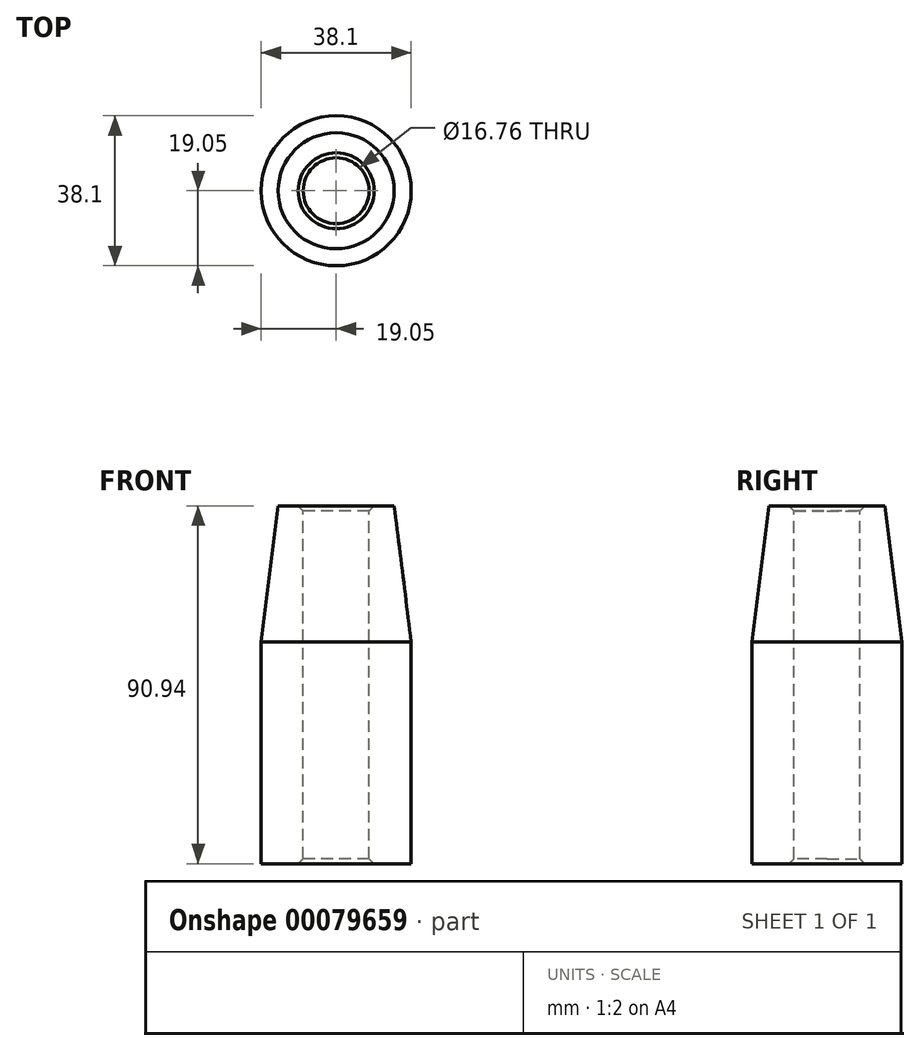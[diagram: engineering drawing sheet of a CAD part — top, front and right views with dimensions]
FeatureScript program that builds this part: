
annotation { "Feature Type Name" : "Feature", "Feature Type Description" : "" }
export const myFeature = defineFeature(function(context is Context, id is Id, definition is map)
    precondition{}
    {
        {
            var Q0;
            Q0=qCreatedBy(makeId("Front.planeOp"),FACE);
            var sketch = newSketch(context, id + "F0", { "sketchPlane" : qUnion([Q0])});
            skLineSegment(sketch, "E0", {"start": v(-8.38, 45.47) * mm, "end": v(-8.38, 0) * mm});
            skLineSegment(sketch, "E1", {"start": v(-8.38, 0) * mm, "end": v(-8.38, -45.47) * mm});
            skLineSegment(sketch, "E2", {"start": v(-19.05, 10.92) * mm, "end": v(-19.05, -45.47) * mm});
            skLineSegment(sketch, "E3", {"start": v(-8.38, 45.47) * mm, "end": v(-14.73, 45.47) * mm});
            skLineSegment(sketch, "E4", {"start": v(-14.73, 45.47) * mm, "end": v(-19.05, 10.92) * mm});
            skLineSegment(sketch, "E5", {"start": v(-19.05, -45.47) * mm, "end": v(-8.38, -45.47) * mm});
            skSolve(sketch);
        }
        {
            var Q0;
            Q0=qCreatedBy(makeId("Front.planeOp"),FACE);
            var sketch = newSketch(context, id + "F1", { "sketchPlane" : qUnion([Q0])});
            skLineSegment(sketch, "E6", {"start": v(0, 53.8) * mm, "end": v(0, -53.5) * mm, "construction": true});
            skSolve(sketch);
        }
        {
            var Q0;
            Q0=makeQuery(id+"F0.imprint","IMPRINT",FACE,{"disambiguationData":[TD([[makeQuery(id+"F0.imprint","IMPRINT",EDGE,{"derivedFrom":sQuery(id+"F0.wireOp",EDGE,"E0")}),-1.0]])]});
            var Q1;
            Q1=sQuery(id+"F1.wireOp",EDGE,"E6");
            revolve(context, id + "F2", {"entities" : qUnion([Q0]), "axis" : qUnion([Q1]), "revolveType" : RevolveType.FULL});
        }
        {
            var Q0;
            Q0=makeQuery(id+"F2.opRevolve","SWEPT_EDGE",EDGE,{"disambiguationData":[OSD([sQuery(id+"F0.wireOp",EDGE,"E0"),sQuery(id+"F0.wireOp",EDGE,"E3")])]});
            chamfer(context, id + "F3", {"entities" : qUnion([Q0]), "width" : 1.27 * mm, "tangentPropagation" : true});
        }
        {
            var Q0;
            Q0=makeQuery(id+"F2.opRevolve","SWEPT_EDGE",EDGE,{"disambiguationData":[OSD([sQuery(id+"F0.wireOp",EDGE,"E1"),sQuery(id+"F0.wireOp",EDGE,"E5")])]});
            chamfer(context, id + "F4", {"entities" : qUnion([Q0]), "width" : 1.27 * mm, "tangentPropagation" : true});
        }
    });
